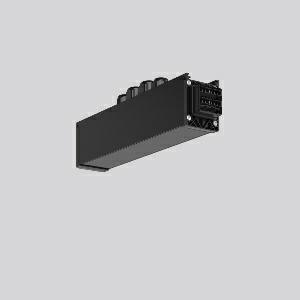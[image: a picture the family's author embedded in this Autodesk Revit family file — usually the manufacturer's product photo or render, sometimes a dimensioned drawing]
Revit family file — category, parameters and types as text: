
# Revit family: linedo_mitteleinspeisung_7pol_982698_003_3_4c1b
name_source: partatom
category: Lighting Fixtures
units: mm (PartAtom-declared; Revit-internal decimal feet)

## family parameters
Cut with Voids When Loaded = No
Host = Face
Light Source = No
Part Type = Normal
Room Calculation Point = No
Round Connector Dimension = Use Diameter
Shared = No

## types (1)
- LINEDO_Mitteleinspeisung_7pol
    Apparent Load = 0 VA
    Default Elevation = 1800 mm
    Description = Series: LINEDO
Middle power feed, 7-pole, connection socket / plug. Housing: extruded aluminium profile, powder-coated. Cover made of plastic, surface like housing. LINEDO plug system, plastic, black. 4 cable glands (2 x M20 and 2 x M25). Cable glands on top. Easy connection for rigid or flexible wires.
Colour: black
Length: 330 mm
Width: 58 mm
Height: 76 mm
Weight: 751 g
    Height = 76 mm
    Lamp = 0 x
    Length = 330 mm
    Luminous efficacy = 0 lm/W
    Manufacturer = RZB
    ModVariant = No
    Model = 982698.003.3
    Mounting Place = Ceiling
    Mounting Type = Surface mounted, Pendant
    Number of Poles = 1
    OnlyDefault = Yes
    Power Factor = 1
    Product Name = LINEDO_Mitteleinspeisung_7pol
    Product group = Surface mounted continuous line luminaire system
    ProductGroupID = 310
    Protection Class = Protection class I
    Protection Degree = IP 54
    RLX_Detail_Level = 1
    RLX_Emergency_Light_Flux = 0 lm
    RLX_Emergency_Type = 0
    RLX_Emergency_Type_DB = No
    RlxData = <blob elided: 23193 chars, md5=5ad8566e>
    Standby Power = 0 W
    System Light Flux = 0 lm
    System Power = 0 W
    Type Comments = Product without accessories
    Type Image = 982698.003.jpg
    URL = http://relux.com
    VarID = ---
    Voltage = 0 V
    Weight = 0.00 kg
    Width = 58 mm

## geometry (parser evidence)
native form markers: Blend x4, Sweep x11
no freeform markers — native parametric forms only
